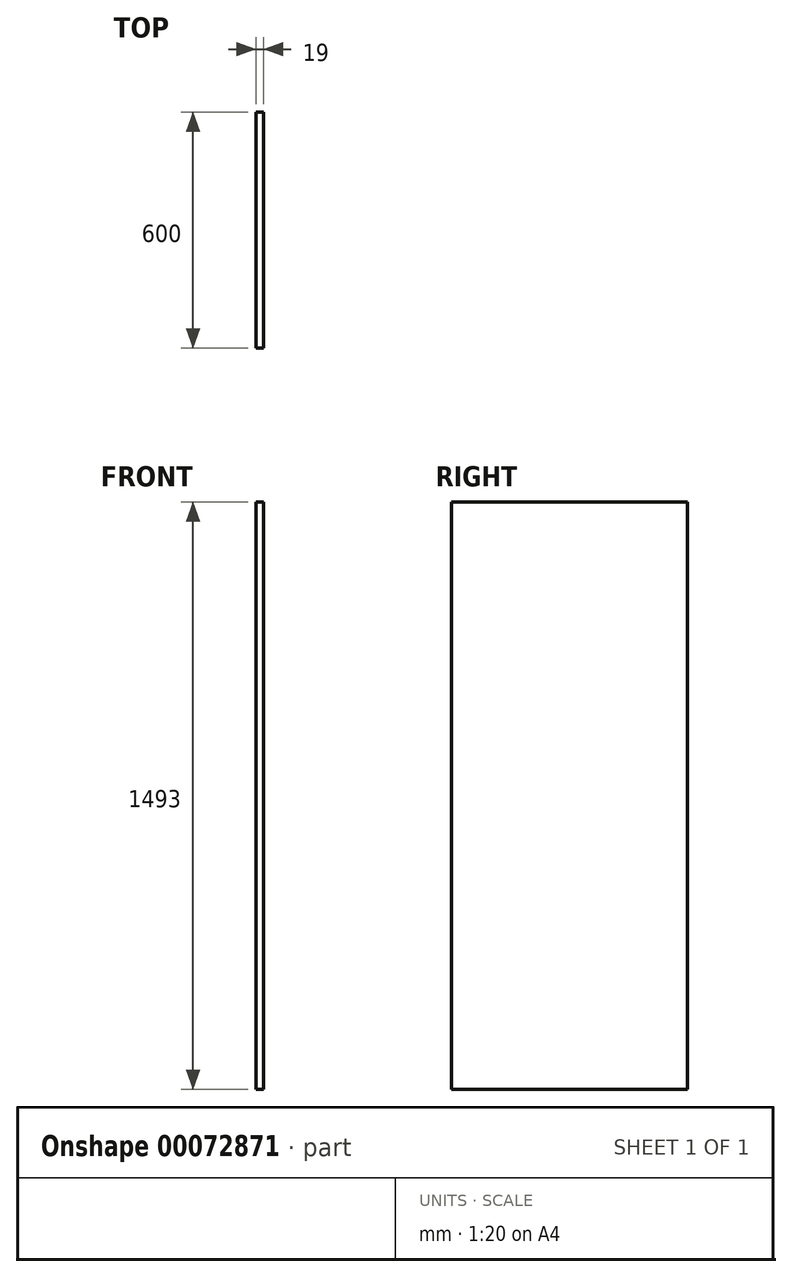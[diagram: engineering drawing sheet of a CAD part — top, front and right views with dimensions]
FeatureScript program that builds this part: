
annotation { "Feature Type Name" : "Feature", "Feature Type Description" : "" }
export const myFeature = defineFeature(function(context is Context, id is Id, definition is map)
    precondition{}
    {
        {
            var Q0;
            Q0=qCreatedBy(makeId("Right.planeOp"),FACE);
            var sketch = newSketch(context, id + "F0", { "sketchPlane" : qUnion([Q0])});
            skLineSegment(sketch, "E0.bottom", {"start": v(0, 0) * mm, "end": v(600, 0) * mm});
            skLineSegment(sketch, "E0.top", {"start": v(0, -1493) * mm, "end": v(600, -1493) * mm});
            skLineSegment(sketch, "E0.left", {"start": v(0, 0) * mm, "end": v(0, -1493) * mm});
            skLineSegment(sketch, "E0.right", {"start": v(600, 0) * mm, "end": v(600, -1493) * mm});
            skSolve(sketch);
        }
        {
            var Q0;
            Q0=makeQuery(id+"F0.imprint","IMPRINT",FACE,{"disambiguationData":[TD([[makeQuery(id+"F0.imprint","IMPRINT",EDGE,{"derivedFrom":sQuery(id+"F0.wireOp",EDGE,"E0.bottom")}),-1.0]])]});
            extrude(context, id + "F1", {"entities" : qUnion([Q0]), "depth" : 19 * mm});
        }
    });
